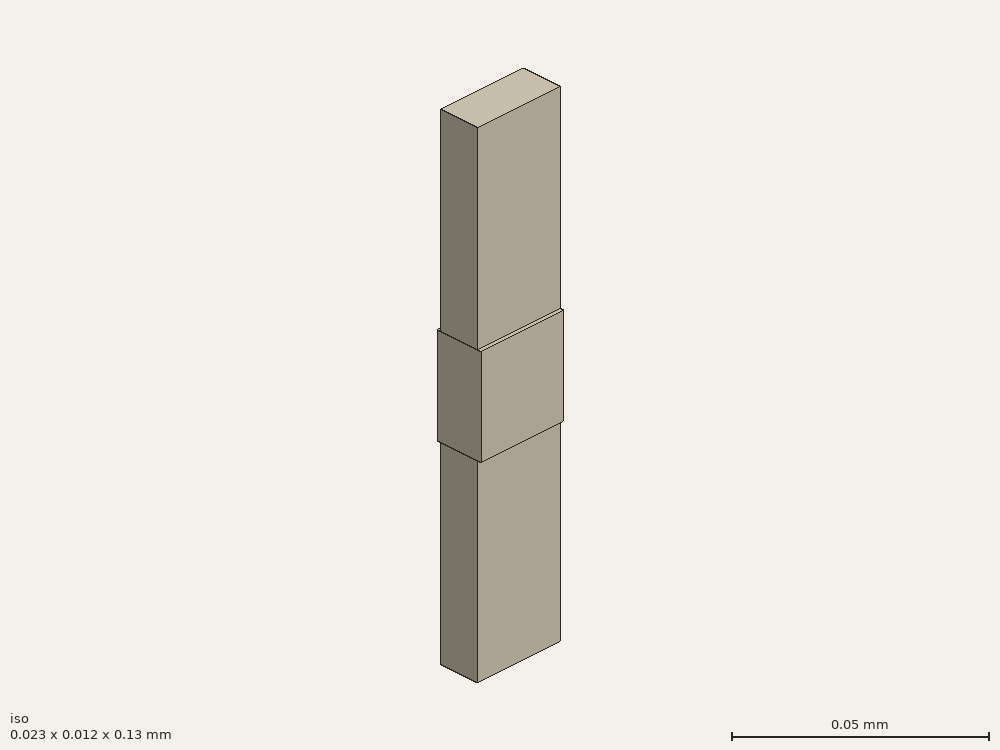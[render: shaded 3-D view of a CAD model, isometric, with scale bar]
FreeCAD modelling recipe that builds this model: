
FCSTD DOCUMENT  (FreeCAD 0.21R33694 (Git))
Label: straight-steps
License: All rights reserved
LicenseURL: http://en.wikipedia.org/wiki/All_rights_reserved
objects: Part::Part2DObjectPython×6, App::FeaturePython×4, Part::FeaturePython×3, Part::Extrusion×2
note: 11 computed .brp shape members not serialized (recipe doc carries the construction recipe); baked Part::Feature solids carry a one-line shape summary decoded from their .brp

FEATURE [Part::Part2DObjectPython] Rectangle  # Draft 2D object (typed FeaturePython)
  Area = 232.258
  ChamferSize = 0
  Columns = 1
  FilletRadius = 0
  Height = 10.16
  Length = 22.86
  MakeFace = true
  Placement = pos=(-11.43,-5.08,0) rot=(0,0,1;0rad)
  Rows = 1
FEATURE [Part::Extrusion] Extrude
  Base = -> Rectangle
  Dir = (0,0,1)
  DirMode = 2
  FaceMakerClass = Part::FaceMakerBullseye
  LengthFwd = 50
  LengthRev = 0
  Solid = false
  Symmetric = false
FEATURE [Part::Part2DObjectPython] Rectangle001  label="_Pport1"  # Draft 2D object (typed FeaturePython)
  Area = 0.000232258
  ChamferSize = 0
  Columns = 1
  FilletRadius = 0
  Height = 0.01016
  Length = 0.02286
  MakeFace = true
  Placement = pos=(-0.01143,-0.00508,0.05) rot=(0,0,1;0rad)
  Rows = 1
FEATURE [Part::Part2DObjectPython] Line  label="_Pv1"  # Draft 2D object (typed FeaturePython)
  Area = 0
  ChamferSize = 0
  Closed = false
  End = (-1.8e-15,0.00508,0.05)
  FilletRadius = 0
  Length = 0.01016
  MakeFace = true
  Placement = pos=(-0.011,-0.005,3e-15) rot=(0,0,1;0rad)
  Points = (2) [(0.011,-8e-05,0.05),(0.011,0.01008,0.05)]
  Start = (0,-0.00508,0.05)
  Subdivisions = 0
FEATURE [App::FeaturePython] Text  label="_S1(PV){port1}"  # WARN: FeaturePython — macro-defined, semantics opaque (R4)
  Placement = pos=(0.0413747,-0.017509,0) rot=(0,0,1;0rad)
  Text = .
FEATURE [App::FeaturePython] Text002  label="_L1(1,voltage){v1}"  # WARN: FeaturePython — macro-defined, semantics opaque (R4)
  Placement = pos=(0.0413747,-0.017509,0) rot=(0,0,1;0rad)
  Text = .
FEATURE [Part::Part2DObjectPython] Rectangle002  # Draft 2D object (typed FeaturePython)
  Area = 277.978
  ChamferSize = 0
  Columns = 1
  FilletRadius = 0
  Height = 22.86
  Length = 12.16
  MakeFace = true
  Placement = pos=(-11.43,-6.08,0) rot=(0.707107,0.707107,0;3.14159rad)
  Rows = 1
FEATURE [Part::Extrusion] Extrude001  label="Extrude002"
  Base = -> Rectangle002
  Dir = (0,0,-1)
  DirMode = 2
  FaceMakerClass = Part::FaceMakerBullseye
  LengthFwd = 25
  LengthRev = 0
  Solid = false
  Symmetric = false
FEATURE [Part::FeaturePython] Clone  label="Extrude003"  # Draft clone (typed FeaturePython)
  AttacherType = Attacher::AttachEngine3D
  Fuse = false
  Objects = -> [Extrude]
  Placement = pos=(0,0,-75) rot=(0,0,1;0rad)
  Scale = (1,1,1)
FEATURE [Part::FeaturePython] BooleanFragments  # WARN: FeaturePython — macro-defined, semantics opaque (R4)
  Mode = 0
  Objects = -> [Extrude,Extrude001,Clone]
  Tolerance = 0
FEATURE [Part::FeaturePython] Clone001  label="scaled"  # Draft clone (typed FeaturePython)
  AttacherType = Attacher::AttachEngine3D
  Fuse = false
  Objects = -> [BooleanFragments]
  Scale = (0.001,0.001,0.001)
FEATURE [Part::Part2DObjectPython] Rectangle003  label="_Pport2"  # Draft 2D object (typed FeaturePython)
  Area = 0.000232258
  ChamferSize = 0
  Columns = 1
  FilletRadius = 0
  Height = 0.02286
  Length = 0.01016
  MakeFace = true
  Placement = pos=(-0.01143,-0.00508,-0.075) rot=(0.707107,0.707107,0;3.14159rad)
  Rows = 1
FEATURE [Part::Part2DObjectPython] Line001  label="_Pv2"  # Draft 2D object (typed FeaturePython)
  Area = 0
  ChamferSize = 0
  Closed = false
  End = (-1.8e-15,0.00508,-0.075)
  FilletRadius = 0
  Length = 0.01016
  MakeFace = true
  Placement = pos=(0,-0.00508,-0.075) rot=(0.707107,0.707107,0;3.14159rad)
  Points = (2) [(0,0,0),(0.01016,-1.77861e-15,2.80331e-15)]
  Start = (0,-0.00508,-0.075)
  Subdivisions = 0
FEATURE [App::FeaturePython] Text003  label="_S2(PV){port2}"  # WARN: FeaturePython — macro-defined, semantics opaque (R4)
  Placement = pos=(0.0413747,-0.017509,0) rot=(0,0,1;0rad)
  Text = .
FEATURE [App::FeaturePython] Text004  label="_L2(2,voltage){v2}"  # WARN: FeaturePython — macro-defined, semantics opaque (R4)
  Placement = pos=(0.0413747,-0.017509,0) rot=(0,0,1;0rad)
  Text = .
